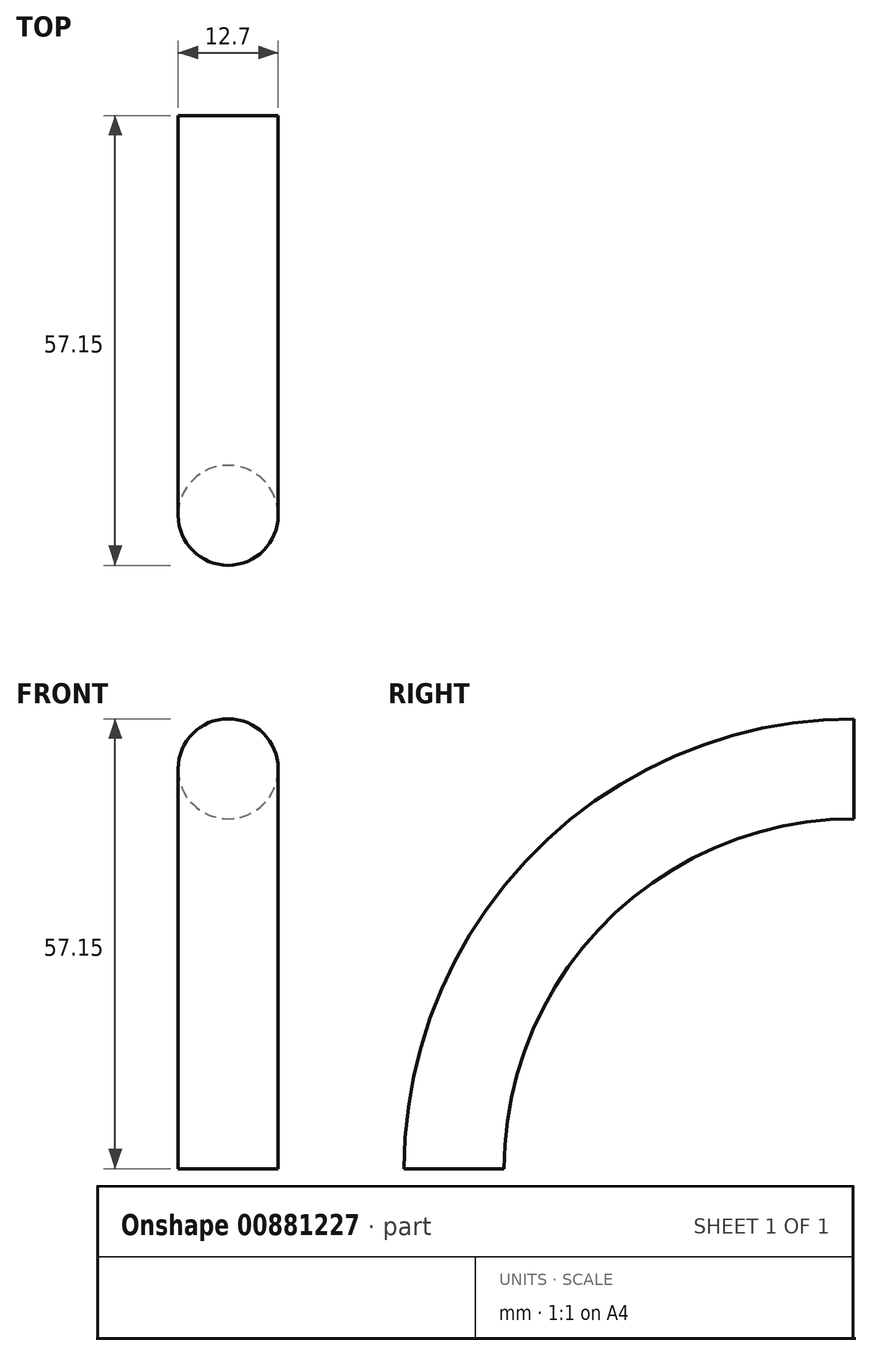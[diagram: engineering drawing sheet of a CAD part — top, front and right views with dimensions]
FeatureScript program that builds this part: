
annotation { "Feature Type Name" : "Feature", "Feature Type Description" : "" }
export const myFeature = defineFeature(function(context is Context, id is Id, definition is map)
    precondition{}
    {
        {
            var Q0;
            Q0=qCreatedBy(makeId("Top.planeOp"),FACE);
            var sketch = newSketch(context, id + "F0", { "sketchPlane" : qUnion([Q0])});
            skCircle(sketch, "E0", {"center": v(0, 0) * mm, "radius": 6.35 * mm});
            skSolve(sketch);
        }
        {
            var Q0;
            Q0=qCreatedBy(makeId("Right.planeOp"),FACE);
            var sketch = newSketch(context, id + "F1", { "sketchPlane" : qUnion([Q0])});
            skArc(sketch, "E1", {"start": v(50.8, 50.8) * mm, "mid": v(14.88, 35.92) * mm, "end": v(0, 0) * mm});
            skSolve(sketch);
        }
        {
            var Q0;
            Q0=makeQuery(id+"F0.imprint","IMPRINT",FACE,{"disambiguationData":[TD([[makeQuery(id+"F0.imprint","IMPRINT",EDGE,{"derivedFrom":sQuery(id+"F0.wireOp",EDGE,"E0")}),1.0]])]});
            var Q1;
            Q1=sQuery(id+"F0.wireOp",EDGE,"E0");
            var Q2;
            Q2=sQuery(id+"F1.wireOp",EDGE,"E1");
            sweep(context, id + "F2", {"bodyType" : ToolBodyType.SURFACE, "profiles" : qUnion([Q0]), "surfaceProfiles" : qUnion([Q1]), "path" : qUnion([Q2])});
        }
    });
